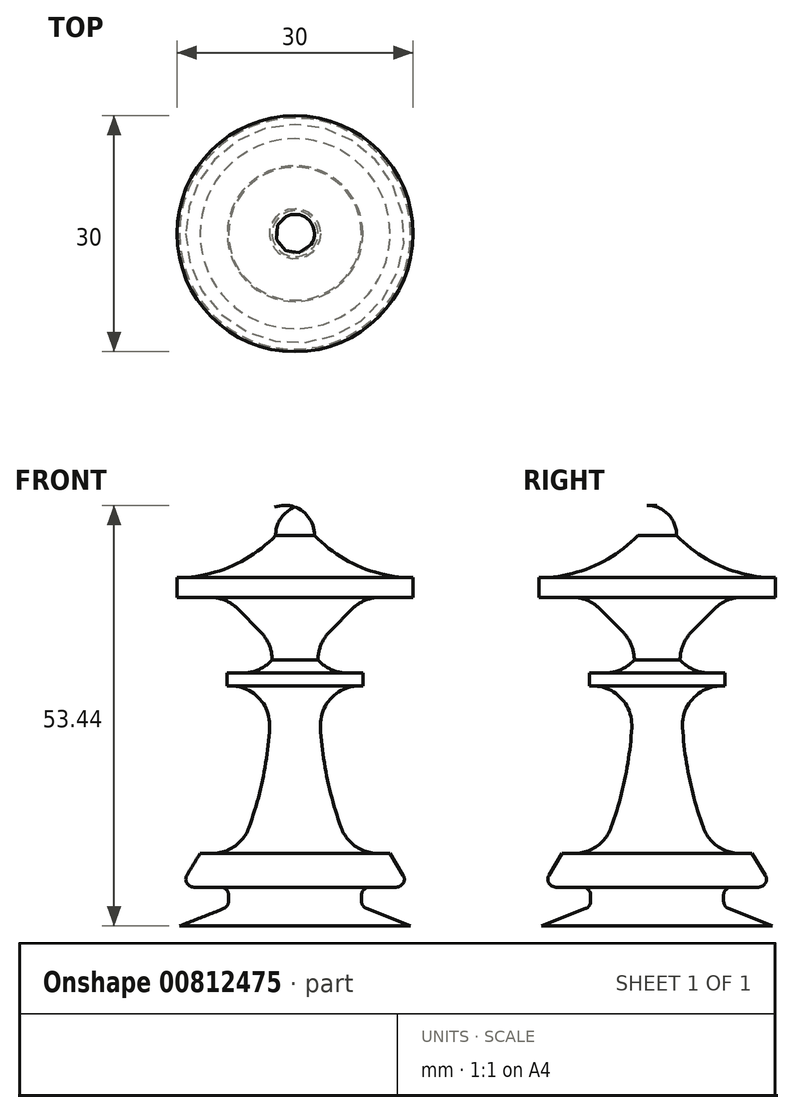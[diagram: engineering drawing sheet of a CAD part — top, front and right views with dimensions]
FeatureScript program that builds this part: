
annotation { "Feature Type Name" : "Feature", "Feature Type Description" : "" }
export const myFeature = defineFeature(function(context is Context, id is Id, definition is map)
    precondition{}
    {
        {
            var Q0;
            Q0=qCreatedBy(makeId("Front.planeOp"),FACE);
            var sketch = newSketch(context, id + "F0", { "sketchPlane" : qUnion([Q0])});
            skLineSegment(sketch, "E0.bottom", {"start": v(0, 0) * mm, "end": v(14.67, 0) * mm});
            skLineSegment(sketch, "E0.left", {"start": v(0, 0) * mm, "end": v(0, 2.45) * mm});
            skLineSegment(sketch, "E1.left", {"start": v(0, 2.45) * mm, "end": v(0, 44.25) * mm});
            skLineSegment(sketch, "E2.top", {"start": v(2.46, 41.74) * mm, "end": v(2.5, 41.74) * mm});
            skLineSegment(sketch, "E2.right", {"start": v(15, 44.25) * mm, "end": v(15, 41.74) * mm});
            skLineSegment(sketch, "E3.right", {"start": v(0, 44.25) * mm, "end": v(0, 49.62) * mm});
            skArc(sketch, "E4", {"start": v(2.46, 49.62) * mm, "mid": v(8.18, 45.65) * mm, "end": v(15, 44.25) * mm});
            skArc(sketch, "E5", {"start": v(2.46, 49.62) * mm, "mid": v(1.8, 51.8) * mm, "end": v(0, 53.2) * mm});
            skLineSegment(sketch, "E6", {"start": v(0, 53.2) * mm, "end": v(0, 49.62) * mm});
            skLineSegment(sketch, "E7", {"start": v(2.91, 35.86) * mm, "end": v(8.73, 41.74) * mm});
            skLineSegment(sketch, "E8.trimOffspring", {"start": v(8.73, 41.74) * mm, "end": v(15, 41.74) * mm});
            skLineSegment(sketch, "E9", {"start": v(8.45, 2.45) * mm, "end": v(8.45, 4.93) * mm});
            skLineSegment(sketch, "E10", {"start": v(8.45, 4.93) * mm, "end": v(14.65, 4.93) * mm});
            skLineSegment(sketch, "E11", {"start": v(14.65, 4.93) * mm, "end": v(12.07, 9.2) * mm});
            skLineSegment(sketch, "E12", {"start": v(2.91, 35.86) * mm, "end": v(2.91, 32.12) * mm});
            skLineSegment(sketch, "E13", {"start": v(2.91, 32.12) * mm, "end": v(8.6, 32.12) * mm});
            skLineSegment(sketch, "E14", {"start": v(8.6, 32.12) * mm, "end": v(8.6, 30.5) * mm});
            skLineSegment(sketch, "E15", {"start": v(8.6, 30.5) * mm, "end": v(3.14, 30.5) * mm});
            skLineSegment(sketch, "E16", {"start": v(3.14, 30.5) * mm, "end": v(3.14, 27.97) * mm});
            skLineSegment(sketch, "E17", {"start": v(12.07, 9.2) * mm, "end": v(7.2, 9.2) * mm});
            skArc(sketch, "E18", {"start": v(3.14, 27.97) * mm, "mid": v(4.17, 18.37) * mm, "end": v(7.2, 9.2) * mm});
            skLineSegment(sketch, "E19", {"start": v(8.45, 2.45) * mm, "end": v(14.67, 0) * mm});
            skSolve(sketch);
        }
        {
            var Q0;
            Q0=makeQuery(id+"F0.imprint","IMPRINT",FACE,{"disambiguationData":[TD([[makeQuery(id+"F0.imprint","IMPRINT",EDGE,{"derivedFrom":sQuery(id+"F0.wireOp",EDGE,"E0.bottom")}),1.0]])]});
            var Q1;
            Q1=sQuery(id+"F0.wireOp",EDGE,"E1.left");
            revolve(context, id + "F1", {"surfaceOperationType" : NewSurfaceOperationType.NEW, "entities" : qUnion([Q0]), "axis" : qUnion([Q1]), "revolveType" : RevolveType.FULL});
        }
        {
            var Q0;
            Q0=makeQuery(id+"F1.opRevolve","SWEPT_FACE",FACE,{"disambiguationData":[OSD([sQuery(id+"F0.wireOp",EDGE,"E7")])]});
            fillet(context, id + "F2", {"entities" : qUnion([Q0]), "radius" : 5 * mm, "tangentPropagation" : true, "allowEdgeOverflow" : false});
        }
        {
            var Q0;
            Q0=makeQuery(id+"F1.opRevolve","SWEPT_FACE",FACE,{"disambiguationData":[OSD([sQuery(id+"F0.wireOp",EDGE,"E12")])]});
            fillet(context, id + "F3", {"entities" : qUnion([Q0]), "radius" : 5 * mm, "tangentPropagation" : true, "allowEdgeOverflow" : false});
        }
        {
            var Q0;
            Q0=makeQuery(id+"F1.opRevolve","SWEPT_FACE",FACE,{"disambiguationData":[OSD([sQuery(id+"F0.wireOp",EDGE,"E16")])]});
            fillet(context, id + "F4", {"entities" : qUnion([Q0]), "radius" : 5 * mm, "tangentPropagation" : true, "allowEdgeOverflow" : false});
        }
        {
            var Q0;
            Q0=makeQuery(id+"F1.opRevolve","SWEPT_FACE",FACE,{"disambiguationData":[OSD([sQuery(id+"F0.wireOp",EDGE,"E18")])]});
            fillet(context, id + "F5", {"entities" : qUnion([Q0]), "radius" : 5 * mm, "tangentPropagation" : true, "allowEdgeOverflow" : false});
        }
        {
            var Q0;
            Q0=makeQuery(id+"F1.opRevolve","SWEPT_FACE",FACE,{"disambiguationData":[OSD([sQuery(id+"F0.wireOp",EDGE,"E9")])]});
            var Q1;
            Q1=makeQuery(id+"F1.opRevolve","SWEPT_EDGE",EDGE,{"disambiguationData":[OSD([sQuery(id+"F0.wireOp",EDGE,"E10"),sQuery(id+"F0.wireOp",EDGE,"E11")])]});
            fillet(context, id + "F6", {"entities" : qUnion([Q0, Q1]), "radius" : 1 * mm, "tangentPropagation" : true, "allowEdgeOverflow" : false});
        }
    });
